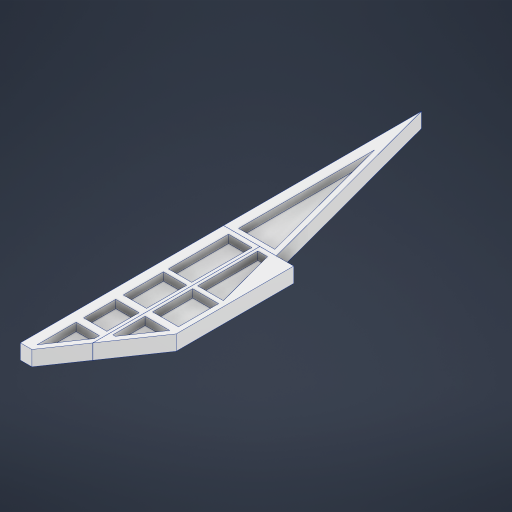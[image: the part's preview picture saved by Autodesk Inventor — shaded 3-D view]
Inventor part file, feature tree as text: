
AUTODESK INVENTOR PART (.ipt)
format: ipt  version: 2024 (Build 280153000, 153)  size: 353,280 bytes
history: native  units: mm
features: extrude x4, sketch x4, projected_geometry x1
ambient origin geometry x8: Origin, YZ Plane, XZ Plane, XY Plane, X Axis, Y Axis, Z Axis, Center Point
bodies: Solid1 (feature_tree)
feature tree (9):
  extrude  "Extrusion1"  Depth=200.0mm
  extrude  "Extrusion2"  Depth=20.0mm
  extrude  "Extrusion3"  Depth=10.0mm
  extrude  "Extrusion6"  Depth=15.0mm
  sketch  "Sketch1"  dims[d0=600.0mm d1=200.0mm]
  sketch  "Sketch2"  dims[d2=160.0mm d3=20.0mm]
  projected_geometry  "Projected Loop1"
  sketch  "Sketch3"  dims[d4=30.0mm d5=0.0mm d6=10.0mm]
  sketch  "Sketch5"  dims[d7=20.0mm d8=15.0mm d9=120.0mm d10=80.0mm d11=10.0mm d12=16.0mm d13=0.0mm d15=15.0mm d16=12.0mm d17=20.0mm d18=20.0mm d19=9.95mm d20=9.95mm d21=5.95mm d22=5.95mm d23=50.0mm d24=0.0mm d29=111.0mm d30=0.0mm]
